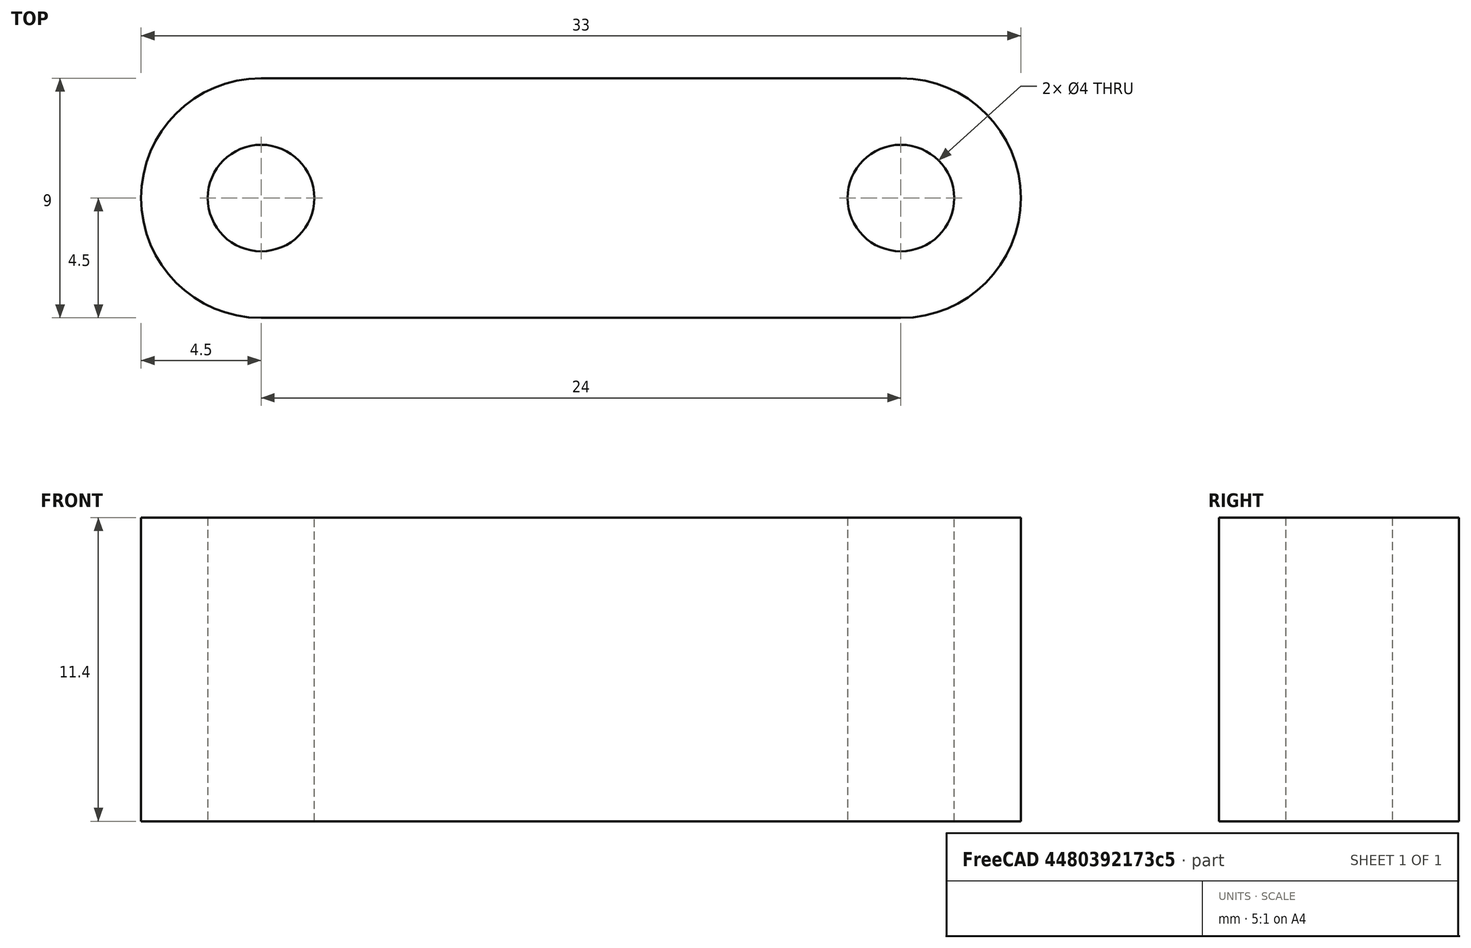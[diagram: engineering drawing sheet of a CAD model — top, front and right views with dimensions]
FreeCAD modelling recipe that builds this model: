
FCSTD DOCUMENT  (FreeCAD 0.14R3700 (Git))
Label: spacers
License: CC-BY 3.0
LicenseURL: http://creativecommons.org/licenses/by/3.0/
objects: Sketcher::SketchObject×1, PartDesign::Pad×1
note: 3 computed .brp shape members not serialized (recipe doc carries the construction recipe); baked Part::Feature solids carry a one-line shape summary decoded from their .brp

FEATURE [Sketcher::SketchObject] Sketch
  sketch-geometry (6):
    g0: ArcOfCircle CenterX=-12 CenterY=0 CenterZ=0 NormalX=0 NormalY=0 NormalZ=1 Radius=4.5 StartAngle=1.57079 EndAngle=4.71239
    g1: ArcOfCircle CenterX=12 CenterY=0 CenterZ=0 NormalX=0 NormalY=0 NormalZ=1 Radius=4.5 StartAngle=4.71239 EndAngle=7.85398
    g2: LineSegment StartX=-12 StartY=-4.5 StartZ=0 EndX=12 EndY=-4.5 EndZ=0
    g3: LineSegment StartX=-12 StartY=4.5 StartZ=0 EndX=12 EndY=4.5 EndZ=0
    g4: Circle CenterX=-12 CenterY=0 CenterZ=0 NormalX=0 NormalY=0 NormalZ=1 Radius=2
    g5: Circle CenterX=12 CenterY=0 CenterZ=0 NormalX=0 NormalY=0 NormalZ=1 Radius=2
  constraints (20):
    c: DistanceX(g-1,g0) = -12
    c: DistanceX(g-1,g1) = 12
    c: Radius(g1) = 4.5
    c: Equal(g1,g0)
    c: Coincident(g0,g3)
    c: Coincident(g0,g2)
    c: Horizontal(g3)
    c: Horizontal(g2)
    c: Coincident(g1,g3)
    c: DistanceY(g-1,g0) = 4.5
    c: DistanceX(g-1,g0) = -12
    c: Equal(g3,g2)
    c: DistanceY(g0,g0) = -4.5
    c: DistanceY(g1,g1) = -4.5
    c: Coincident(g1,g2)
    c: Radius(g4) = 2
    c: Coincident(g0,g4)
    c: Radius(g5) = 2
    c: Coincident(g1,g5)
    c: Coincident(g0,g3)
FEATURE [PartDesign::Pad] Pad
  Length = 11.4
  Length2 = 20
  Sketch = -> Sketch
  Type = 0
